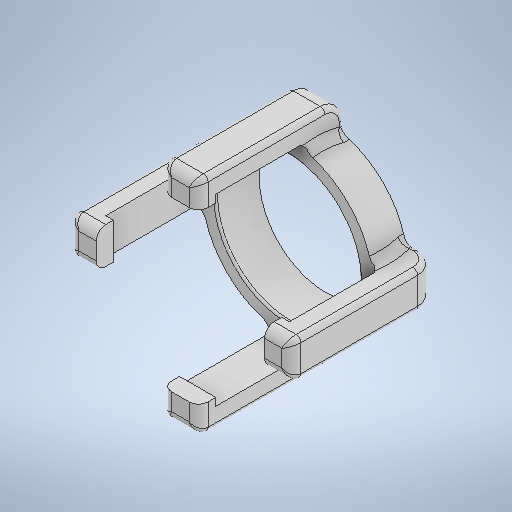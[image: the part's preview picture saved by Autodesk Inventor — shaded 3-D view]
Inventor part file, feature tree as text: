
AUTODESK INVENTOR PART (.ipt)
format: ipt  version: 2025.1 (Build 291241000, 241)  size: 653,824 bytes
history: native  units: mm
features: sketch x9, extrude x7, fillet x5, revolve x2, plane x1, chamfer x1
ambient origin geometry x8: Origin, YZ Plane, XZ Plane, XY Plane, X Axis, Y Axis, Z Axis, Center Point
bodies: Volumenkörper1 (feature_tree)
feature tree (25):
  revolve  "Umdrehung1"
  revolve  "Umdrehung2"
  extrude  "Extrusion1"  Depth=18.0mm
  plane  "Arbeitsebene3"
  extrude  "Extrusion2"  Depth=9.0mm
  extrude  "Extrusion3"  TaperAngle=0.0deg  [1 undecoded]
  extrude  "Extrusion9"  Depth=15.15mm
  extrude  "Extrusion10"  Depth=7.575mm
  extrude  "Extrusion11"  Depth=4.0mm
  extrude  "Extrusion12"  Depth=30.0mm TaperAngle=0.0deg
  fillet  "Rundung5"  Radius=15.0mm
  fillet  "Rundung8"  Radius=15.0mm
  fillet  "Rundung9"  Radius=3.0mm
  fillet  "Rundung10"  Radius=15.2mm
  fillet  "Rundung11"  Radius=14.2mm
  chamfer  "Fasen6"  Distance=11.6mm
  sketch  "Skizze2"  dims[d2=9.0mm d3=18.0mm]
  sketch  "Skizze3"  dims[d4=9.0mm d5=9.0mm]
  sketch  "Skizze4"  dims[d6=90.0deg d7=0.0mm]
  sketch  "Skizze5"  dims[d8=7.575mm d9=15.15mm]
  sketch  "Skizze6"  dims[d10=7.575mm d11=7.575mm]
  sketch  "Skizze13"  dims[d12=90.0deg d13=4.0mm]
  sketch  "Skizze14"  dims[d14=1.0mm d15=30.0mm d16=0.0mm d17=15.0mm d18=15.0mm d19=3.0mm d22=15.2mm d23=0.0mm d28=14.2mm d29=0.0mm]
  sketch  "Skizze15"  dims[d61=0.2mm]
  sketch  "Skizze16"  dims[d66=3.8mm d67=11.6mm d72=1.8mm d73=0.8mm d74=0.0mm d75=1.8mm d76=0.8mm d77=0.0mm d78=1.8mm d79=0.8mm d80=0.0mm d81=1.8mm d82=0.8mm d83=0.0mm d84=2.0mm d85=0.5mm d86=1.0mm d87=1.0mm d88=0.5mm d89=2.0mm d90=45.0deg d30=0.5mm d31=0.872665mm d32=0.5mm d33=0.872665mm d45=0.0mm d46=0.0mm d47=0.0mm d48=0.0mm]
note: 1 required parameter value undecoded (feature->parameter linkage not recoverable at this tier; creation-order binding heuristic only, values carry confidence <= 0.55)
